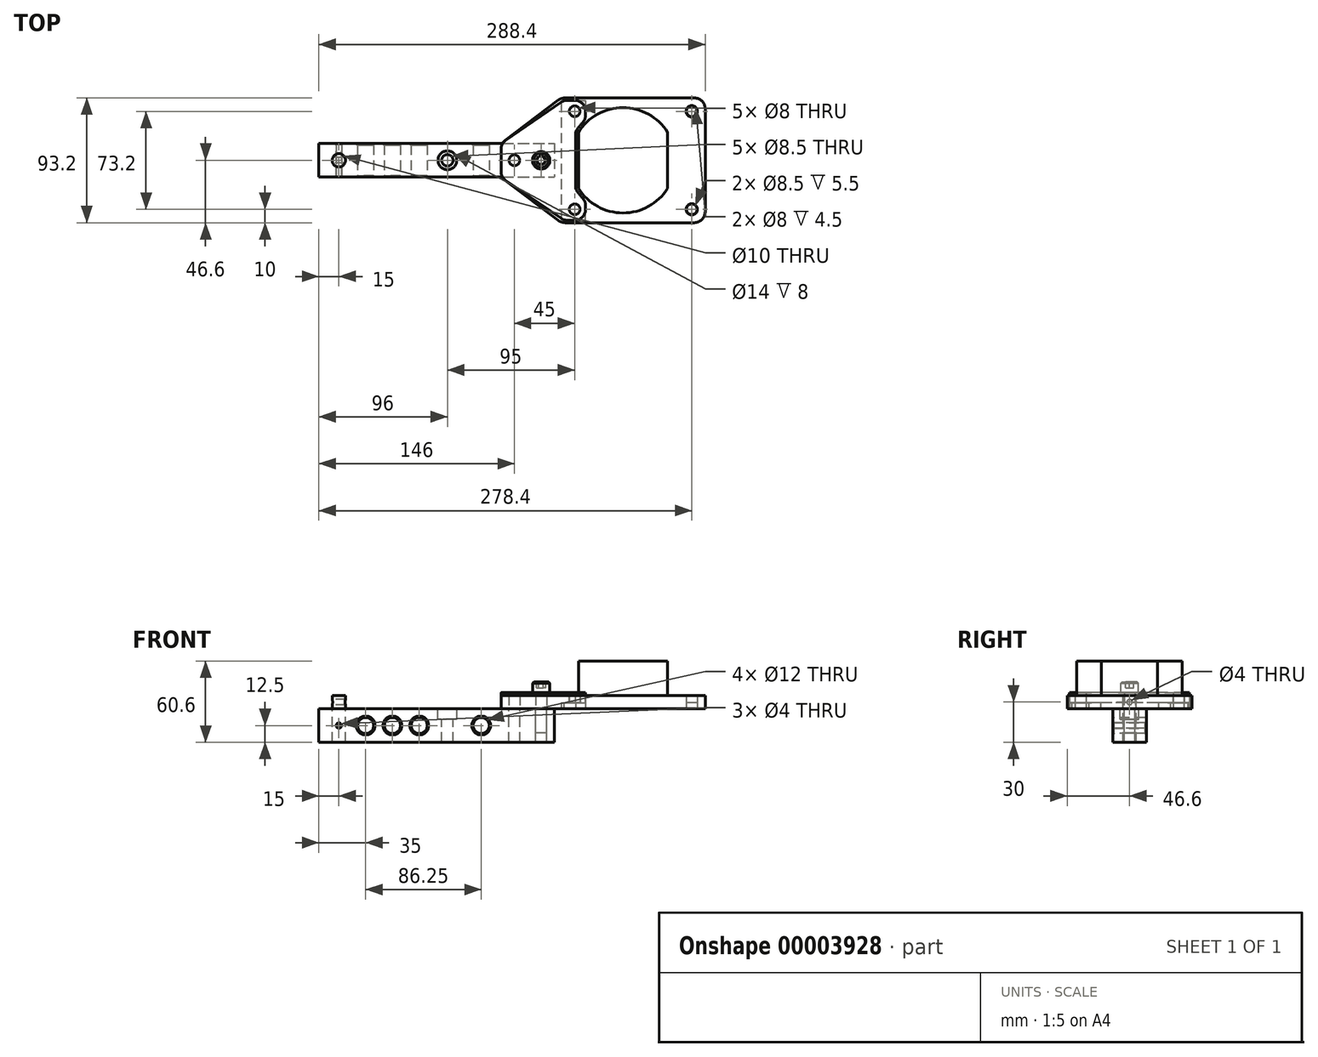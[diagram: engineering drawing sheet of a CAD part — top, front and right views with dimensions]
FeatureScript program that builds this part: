
annotation { "Feature Type Name" : "Feature", "Feature Type Description" : "" }
export const myFeature = defineFeature(function(context is Context, id is Id, definition is map)
    precondition{}
    {
        {
            var Q0;
            Q0=qCreatedBy(makeId("Top.planeOp"),FACE);
            var sketch = newSketch(context, id + "F0", { "sketchPlane" : qUnion([Q0])});
            skLineSegment(sketch, "E0.bottom", {"start": v(-166, 12.5) * mm, "end": v(10, 12.5) * mm});
            skLineSegment(sketch, "E0.left", {"start": v(-166, 12.5) * mm, "end": v(-166, -12.5) * mm});
            skCircle(sketch, "E1", {"center": v(0, 0) * mm, "radius": 4 * mm});
            skCircle(sketch, "E2", {"center": v(-20, 0) * mm, "radius": 4 * mm});
            skLineSegment(sketch, "E3", {"start": v(-166, -12.5) * mm, "end": v(10, -12.5) * mm});
            skLineSegment(sketch, "E4", {"start": v(10, 12.5) * mm, "end": v(10, 0) * mm});
            skLineSegment(sketch, "E5", {"start": v(10, 0) * mm, "end": v(10, -12.5) * mm});
            skCircle(sketch, "E6", {"center": v(-151, 0) * mm, "radius": 5 * mm});
            skCircle(sketch, "E7", {"center": v(-70, 0) * mm, "radius": 4.25 * mm});
            skCircle(sketch, "E8", {"center": v(-70, 0) * mm, "radius": 7 * mm});
            skSolve(sketch);
        }
        {
            var Q0;
            Q0 = qSketchRegion(id + "F0", true);
            var Q1;
            Q1=makeQuery(id+"F0.imprint","IMPRINT",FACE,{"disambiguationData":[TD([[makeQuery(id+"F0.imprint","IMPRINT",EDGE,{"derivedFrom":sQuery(id+"F0.wireOp",EDGE,"E7")}),-1.0]])]});
            extrude(context, id + "F1", {"entities" : qUnion([Q0, Q1]), "oppositeDirection" : true, "depth" : 25 * mm});
        }
        {
            var Q0;
            Q0=makeQuery(id+"F0.imprint","IMPRINT",FACE,{"disambiguationData":[TD([[makeQuery(id+"F0.imprint","IMPRINT",EDGE,{"derivedFrom":sQuery(id+"F0.wireOp",EDGE,"E7")}),-1.0]])]});
            extrude(context, id + "F2", {"entities" : qUnion([Q0]), "operationType" : NewBodyOperationType.REMOVE, "oppositeDirection" : true, "depth" : 8 * mm});
        }
        {
            var Q0;
            Q0=qCreatedBy(makeId("Front.planeOp"),FACE);
            var sketch = newSketch(context, id + "F3", { "sketchPlane" : qUnion([Q0])});
            skLineSegment(sketch, "E9.0", {"start": v(-156, 0) * mm, "end": v(-146, 0) * mm, "construction": true});
            skPoint(sketch, "E10", {"position": v(-151, 0) * mm});
            skCircle(sketch, "E11", {"center": v(-151, -12.5) * mm, "radius": 2 * mm});
            skLineSegment(sketch, "E12", {"start": v(-63, 0) * mm, "end": v(-63, -8) * mm});
            skLineSegment(sketch, "E13", {"start": v(-77, -8) * mm, "end": v(-77, 0) * mm});
            skLineSegment(sketch, "E14.0.0", {"start": v(-77, -8) * mm, "end": v(-63, -8) * mm});
            skLineSegment(sketch, "E15", {"start": v(-65.75, -8) * mm, "end": v(-65.75, -25) * mm});
            skLineSegment(sketch, "E16", {"start": v(-74.25, -25) * mm, "end": v(-74.25, -8) * mm});
            skLineSegment(sketch, "E17", {"start": v(-16, 0) * mm, "end": v(-16, -25) * mm});
            skLineSegment(sketch, "E18", {"start": v(-24, -25) * mm, "end": v(-24, 0) * mm});
            skLineSegment(sketch, "E19", {"start": v(4, 0) * mm, "end": v(4, -25) * mm});
            skLineSegment(sketch, "E20", {"start": v(-4, -25) * mm, "end": v(-4, 0) * mm});
            skCircle(sketch, "E21", {"center": v(-44.75, -12.5) * mm, "radius": 6 * mm});
            skCircle(sketch, "E22", {"center": v(-91, -12.5) * mm, "radius": 6 * mm});
            skCircle(sketch, "E23", {"center": v(-111, -12.5) * mm, "radius": 6 * mm});
            skLineSegment(sketch, "E24.0.0", {"start": v(10, 0) * mm, "end": v(-166, 0) * mm});
            skLineSegment(sketch, "E24.0.2", {"start": v(-166, 0) * mm, "end": v(10, 0) * mm});
            skLineSegment(sketch, "E25.0.0", {"start": v(-166, -25) * mm, "end": v(10, -25) * mm});
            skLineSegment(sketch, "E25.0.2", {"start": v(10, -25) * mm, "end": v(-166, -25) * mm});
            skLineSegment(sketch, "E26.0.1", {"start": v(-166, 0) * mm, "end": v(-166, -25) * mm});
            skLineSegment(sketch, "E26.0.3", {"start": v(-166, -25) * mm, "end": v(-166, 0) * mm});
            skLineSegment(sketch, "E27.0.1", {"start": v(10, 0) * mm, "end": v(10, -25) * mm});
            skLineSegment(sketch, "E27.0.3", {"start": v(10, -25) * mm, "end": v(10, 0) * mm});
            skLineSegment(sketch, "E28", {"start": v(-166, -12.5) * mm, "end": v(10, -12.5) * mm, "construction": true});
            skLineSegment(sketch, "E29", {"start": v(-146, 0) * mm, "end": v(-146, -25) * mm});
            skLineSegment(sketch, "E30", {"start": v(-156, -25) * mm, "end": v(-156, 0) * mm});
            skCircle(sketch, "E31", {"center": v(-131, -12.5) * mm, "radius": 6 * mm});
            skSolve(sketch);
        }
        {
            var Q0;
            Q0=makeQuery(id+"F3.imprint","IMPRINT",FACE,{"disambiguationData":[TD([[makeQuery(id+"F3.imprint","IMPRINT",EDGE,{"derivedFrom":sQuery(id+"F3.wireOp",EDGE,"E11")}),1.0]])]});
            var Q1;
            Q1=makeQuery(id+"F3.imprint","IMPRINT",FACE,{"disambiguationData":[TD([[makeQuery(id+"F3.imprint","IMPRINT",EDGE,{"derivedFrom":sQuery(id+"F3.wireOp",EDGE,"E23")}),1.0]])]});
            var Q2;
            Q2=makeQuery(id+"F3.imprint","IMPRINT",FACE,{"disambiguationData":[TD([[makeQuery(id+"F3.imprint","IMPRINT",EDGE,{"derivedFrom":sQuery(id+"F3.wireOp",EDGE,"E22")}),1.0]])]});
            var Q3;
            Q3=makeQuery(id+"F3.imprint","IMPRINT",FACE,{"disambiguationData":[TD([[makeQuery(id+"F3.imprint","IMPRINT",EDGE,{"derivedFrom":sQuery(id+"F3.wireOp",EDGE,"E21")}),1.0]])]});
            var Q4;
            Q4=makeQuery(id+"F3.imprint","IMPRINT",FACE,{"disambiguationData":[TD([[makeQuery(id+"F3.imprint","IMPRINT",EDGE,{"derivedFrom":sQuery(id+"F3.wireOp",EDGE,"E31")}),1.0]])]});
            extrude(context, id + "F4", {"entities" : qUnion([Q0, Q1, Q2, Q3, Q4]), "operationType" : NewBodyOperationType.REMOVE, "oppositeDirection" : true, "depth" : 25 * mm, "hasSecondDirection" : true, "secondDirectionOppositeDirection" : false, "secondDirectionDepth" : 25 * mm});
        }
        {
            var Q0;
            Q0=qCreatedBy(makeId("Top.planeOp"),FACE);
            var sketch = newSketch(context, id + "F5", { "sketchPlane" : qUnion([Q0])});
            skCircle(sketch, "E32", {"center": v(112.4, 36.6) * mm, "radius": 4.25 * mm});
            skCircle(sketch, "E33", {"center": v(112.4, -36.6) * mm, "radius": 4.25 * mm});
            skCircle(sketch, "E34", {"center": v(25, -36.6) * mm, "radius": 4.25 * mm});
            skCircle(sketch, "E35", {"center": v(25, 36.6) * mm, "radius": 4.25 * mm});
            skCircle(sketch, "E36", {"center": v(0, 0) * mm, "radius": 4.25 * mm});
            skCircle(sketch, "E37", {"center": v(-20, 0) * mm, "radius": 4.25 * mm});
            skLineSegment(sketch, "E38", {"start": v(25, 0) * mm, "end": v(25, 36.6) * mm, "construction": true});
            skLineSegment(sketch, "E39", {"start": v(25, 0) * mm, "end": v(25, -36.6) * mm, "construction": true});
            skLineSegment(sketch, "E40", {"start": v(25, 36.6) * mm, "end": v(112.4, 36.6) * mm, "construction": true});
            skLineSegment(sketch, "E41", {"start": v(112.4, 36.6) * mm, "end": v(112.4, -36.6) * mm, "construction": true});
            skLineSegment(sketch, "E42", {"start": v(112.4, -36.6) * mm, "end": v(25, -36.6) * mm, "construction": true});
            skLineSegment(sketch, "E43.bottom", {"start": v(17.69, 46.6) * mm, "end": v(114.4, 46.6) * mm});
            skLineSegment(sketch, "E43.top", {"start": v(17.69, -46.6) * mm, "end": v(114.4, -46.6) * mm});
            skLineSegment(sketch, "E43.right", {"start": v(122.4, 38.6) * mm, "end": v(122.4, -38.6) * mm});
            skLineSegment(sketch, "E44", {"start": v(15, 46.6) * mm, "end": v(15, 0) * mm, "construction": true});
            skLineSegment(sketch, "E45", {"start": v(15, 0) * mm, "end": v(15, -46.6) * mm, "construction": true});
            skLineSegment(sketch, "E46", {"start": v(-30, 0) * mm, "end": v(-30, 8.52) * mm});
            skLineSegment(sketch, "E47", {"start": v(-30, 0) * mm, "end": v(-30, -8.52) * mm});
            skLineSegment(sketch, "E48", {"start": v(-26.83, 14.9) * mm, "end": v(12.86, 44.98) * mm});
            skLineSegment(sketch, "E49", {"start": v(-26.83, -14.9) * mm, "end": v(12.86, -44.98) * mm});
            skPoint(sketch, "E50.visualSharp", {"position": v(122.4, 46.6) * mm});
            skArc(sketch, "E50.filletArc", {"start": v(122.4, 38.6) * mm, "mid": v(120.06, 44.26) * mm, "end": v(114.4, 46.6) * mm});
            skPoint(sketch, "E51.visualSharp", {"position": v(15, 46.6) * mm});
            skArc(sketch, "E51.filletArc", {"start": v(17.69, 46.6) * mm, "mid": v(15.14, 46.18) * mm, "end": v(12.86, 44.98) * mm});
            skPoint(sketch, "E52.visualSharp", {"position": v(-30, 12.5) * mm});
            skArc(sketch, "E52.filletArc", {"start": v(-26.83, 14.9) * mm, "mid": v(-29.16, 12.08) * mm, "end": v(-30, 8.52) * mm});
            skPoint(sketch, "E53.visualSharp", {"position": v(-30, -12.5) * mm});
            skArc(sketch, "E53.filletArc", {"start": v(-30, -8.52) * mm, "mid": v(-29.16, -12.08) * mm, "end": v(-26.83, -14.9) * mm});
            skPoint(sketch, "E54.visualSharp", {"position": v(15, -46.6) * mm});
            skArc(sketch, "E54.filletArc", {"start": v(12.86, -44.98) * mm, "mid": v(15.14, -46.18) * mm, "end": v(17.69, -46.6) * mm});
            skPoint(sketch, "E55.visualSharp", {"position": v(122.4, -46.6) * mm});
            skArc(sketch, "E55.filletArc", {"start": v(114.4, -46.6) * mm, "mid": v(120.06, -44.26) * mm, "end": v(122.4, -38.6) * mm});
            skSolve(sketch);
        }
        {
            var Q0;
            Q0 = qSketchRegion(id + "F5", true);
            extrude(context, id + "F6", {"entities" : qUnion([Q0]), "depth" : 10 * mm});
        }
        {
            var Q0;
            Q0=qCreatedBy(makeId("Top.planeOp"),FACE);
            var sketch = newSketch(context, id + "F7", { "sketchPlane" : qUnion([Q0])});
            skLineSegment(sketch, "E56", {"start": v(0, 0) * mm, "end": v(133.67, 0) * mm, "construction": true});
            skPoint(sketch, "E57.0", {"position": v(112.4, 36.6) * mm});
            skPoint(sketch, "E57.1", {"position": v(112.4, -36.6) * mm});
            skPoint(sketch, "E57.2", {"position": v(25, -36.6) * mm});
            skPoint(sketch, "E57.3", {"position": v(25, 36.6) * mm});
            skCircle(sketch, "E58", {"center": v(25, 36.6) * mm, "radius": 4 * mm});
            skCircle(sketch, "E59", {"center": v(112.4, 36.6) * mm, "radius": 4 * mm});
            skCircle(sketch, "E60", {"center": v(112.4, -36.6) * mm, "radius": 4 * mm});
            skCircle(sketch, "E61", {"center": v(25, -36.6) * mm, "radius": 4 * mm});
            skLineSegment(sketch, "E62", {"start": v(25, 36.6) * mm, "end": v(112.4, 36.6) * mm, "construction": true});
            skLineSegment(sketch, "E63", {"start": v(25, 36.6) * mm, "end": v(25, 0) * mm, "construction": true});
            skLineSegment(sketch, "E64", {"start": v(25, 0) * mm, "end": v(25, -36.6) * mm, "construction": true});
            skLineSegment(sketch, "E65", {"start": v(25, -36.6) * mm, "end": v(112.4, -36.6) * mm, "construction": true});
            skLineSegment(sketch, "E66", {"start": v(112.4, -36.6) * mm, "end": v(112.4, 36.6) * mm, "construction": true});
            skLineSegment(sketch, "E67.bottom", {"start": v(24.85, 44.75) * mm, "end": v(112.55, 44.75) * mm});
            skLineSegment(sketch, "E67.top", {"start": v(24.85, -44.75) * mm, "end": v(112.55, -44.75) * mm});
            skLineSegment(sketch, "E67.left", {"start": v(16.85, 36.75) * mm, "end": v(16.85, -36.75) * mm});
            skLineSegment(sketch, "E67.right", {"start": v(120.55, 36.75) * mm, "end": v(120.55, -36.75) * mm});
            skPoint(sketch, "E68.visualSharp", {"position": v(16.85, 44.75) * mm});
            skArc(sketch, "E68.filletArc", {"start": v(24.85, 44.75) * mm, "mid": v(19.2, 42.4) * mm, "end": v(16.85, 36.75) * mm});
            skPoint(sketch, "E69.visualSharp", {"position": v(120.55, 44.75) * mm});
            skArc(sketch, "E69.filletArc", {"start": v(120.55, 36.75) * mm, "mid": v(118.2, 42.4) * mm, "end": v(112.55, 44.75) * mm});
            skPoint(sketch, "E70.visualSharp", {"position": v(120.55, -44.75) * mm});
            skArc(sketch, "E70.filletArc", {"start": v(112.55, -44.75) * mm, "mid": v(118.2, -42.4) * mm, "end": v(120.55, -36.75) * mm});
            skPoint(sketch, "E71.visualSharp", {"position": v(16.85, -44.75) * mm});
            skArc(sketch, "E71.filletArc", {"start": v(16.85, -36.75) * mm, "mid": v(19.2, -42.4) * mm, "end": v(24.85, -44.75) * mm});
            skPoint(sketch, "E72", {"position": v(61.1, 0) * mm});
            skCircle(sketch, "E73", {"center": v(61.1, 0) * mm, "radius": 39.35 * mm});
            skLineSegment(sketch, "E74", {"start": v(27.8, 20.97) * mm, "end": v(27.8, -20.97) * mm});
            skLineSegment(sketch, "E75", {"start": v(94.4, 20.97) * mm, "end": v(94.4, -20.97) * mm});
            skSolve(sketch);
        }
        {
            var Q0;
            Q0=makeQuery(id+"F7.imprint","IMPRINT",FACE,{"disambiguationData":[TD([[makeQuery(id+"F7.imprint","IMPRINT",EDGE,{"derivedFrom":sQuery(id+"F7.wireOp",EDGE,"E58")}),-1.0]])]});
            var Q1;
            {var subQ0=sQuery(id+"F7.wireOp",EDGE,"E74");Q1=makeQuery(id+"F7.imprint","IMPRINT",FACE,{"disambiguationData":[TD([[makeQuery(id+"F7.imprint","IMPRINT",EDGE,{"derivedFrom":subQ0}),-1.0]])]});}
            var Q2;
            {var subQ0=sQuery(id+"F7.wireOp",EDGE,"E75");Q2=makeQuery(id+"F7.imprint","IMPRINT",FACE,{"disambiguationData":[TD([[makeQuery(id+"F7.imprint","IMPRINT",EDGE,{"derivedFrom":subQ0}),1.0]])]});}
            var Q3;
            {var subQ1=sQuery(id+"F7.wireOp",EDGE,"E74");Q3=makeQuery(id+"F7.imprint","IMPRINT",FACE,{"disambiguationData":[TD([[makeQuery(id+"F7.imprint","IMPRINT",EDGE,{"derivedFrom":subQ1}),1.0]])]});}
            extrude(context, id + "F8", {"entities" : qUnion([Q0, Q1, Q2, Q3]), "depth" : 4.5 * mm});
        }
        {
            var Q0;
            {var subQ1=sQuery(id+"F7.wireOp",EDGE,"E74");Q0=makeQuery(id+"F7.imprint","IMPRINT",FACE,{"disambiguationData":[TD([[makeQuery(id+"F7.imprint","IMPRINT",EDGE,{"derivedFrom":subQ1}),1.0]])]});}
            extrude(context, id + "F9", {"entities" : qUnion([Q0]), "operationType" : NewBodyOperationType.ADD, "depth" : 35.6 * mm});
        }
        {
            var Q0;
            Q0=qCreatedBy(makeId("Top.planeOp"),FACE);
            var sketch = newSketch(context, id + "F10", { "sketchPlane" : qUnion([Q0])});
            skPoint(sketch, "E76.0", {"position": v(25, 36.6) * mm});
            skPoint(sketch, "E76.1", {"position": v(25, -36.6) * mm});
            skPoint(sketch, "E76.2", {"position": v(0, 0) * mm});
            skCircle(sketch, "E77", {"center": v(0, 0) * mm, "radius": 4 * mm});
            skCircle(sketch, "E78", {"center": v(25, 36.6) * mm, "radius": 4 * mm});
            skCircle(sketch, "E79", {"center": v(25, -36.6) * mm, "radius": 4 * mm});
            skCircle(sketch, "E80", {"center": v(-20, 0) * mm, "radius": 4 * mm});
            skLineSegment(sketch, "E81", {"start": v(-30, 0) * mm, "end": v(-30, 12.5) * mm});
            skLineSegment(sketch, "E82", {"start": v(-30, 0) * mm, "end": v(-30, -12.5) * mm});
            skLineSegment(sketch, "E83", {"start": v(-30, 12.5) * mm, "end": v(16.85, 44.75) * mm});
            skLineSegment(sketch, "E84", {"start": v(16.85, 44.75) * mm, "end": v(33.15, 44.75) * mm});
            skLineSegment(sketch, "E85", {"start": v(-30, 0) * mm, "end": v(40.55, 0) * mm, "construction": true});
            skLineSegment(sketch, "E86", {"start": v(33.15, 44.75) * mm, "end": v(33.15, 0) * mm});
            skLineSegment(sketch, "E87.0.MirrorCS", {"start": v(33.15, -44.75) * mm, "end": v(33.15, 0) * mm});
            skLineSegment(sketch, "E87.1.MirrorCS", {"start": v(-30, -12.5) * mm, "end": v(16.85, -44.75) * mm});
            skLineSegment(sketch, "E87.2.MirrorCS", {"start": v(16.85, -44.75) * mm, "end": v(33.15, -44.75) * mm});
            skArc(sketch, "E88.0.0", {"start": v(94.4, 20.97) * mm, "mid": v(61.1, 39.35) * mm, "end": v(27.8, 20.97) * mm});
            skLineSegment(sketch, "E88.0.1", {"start": v(27.8, 20.97) * mm, "end": v(27.8, -20.97) * mm});
            skArc(sketch, "E88.0.2", {"start": v(27.8, -20.97) * mm, "mid": v(61.1, -39.35) * mm, "end": v(94.4, -20.97) * mm});
            skLineSegment(sketch, "E88.0.3", {"start": v(94.4, 20.97) * mm, "end": v(94.4, -20.97) * mm});
            skLineSegment(sketch, "E88.1.0", {"start": v(24.85, 44.75) * mm, "end": v(112.55, 44.75) * mm});
            skArc(sketch, "E88.1.1", {"start": v(24.85, 44.75) * mm, "mid": v(19.2, 42.4) * mm, "end": v(16.85, 36.75) * mm});
            skLineSegment(sketch, "E88.1.2", {"start": v(16.85, 36.75) * mm, "end": v(16.85, -36.75) * mm});
            skArc(sketch, "E88.1.3", {"start": v(16.85, -36.75) * mm, "mid": v(19.2, -42.4) * mm, "end": v(24.85, -44.75) * mm});
            skLineSegment(sketch, "E88.1.4", {"start": v(24.85, -44.75) * mm, "end": v(112.55, -44.75) * mm});
            skArc(sketch, "E88.1.5", {"start": v(112.55, -44.75) * mm, "mid": v(118.2, -42.4) * mm, "end": v(120.55, -36.75) * mm});
            skLineSegment(sketch, "E88.1.6", {"start": v(120.55, 36.75) * mm, "end": v(120.55, -36.75) * mm});
            skArc(sketch, "E88.1.7", {"start": v(120.55, 36.75) * mm, "mid": v(118.2, 42.4) * mm, "end": v(112.55, 44.75) * mm});
            skLineSegment(sketch, "E89.0", {"start": v(25.8, 21.53) * mm, "end": v(25.8, -21.53) * mm});
            skArc(sketch, "E89.1", {"start": v(96.4, 21.53) * mm, "mid": v(61.1, 41.35) * mm, "end": v(25.8, 21.53) * mm});
            skLineSegment(sketch, "E89.2", {"start": v(96.4, 21.53) * mm, "end": v(96.4, -21.53) * mm});
            skArc(sketch, "E89.3", {"start": v(25.8, -21.53) * mm, "mid": v(61.1, -41.35) * mm, "end": v(96.4, -21.53) * mm});
            skLineSegment(sketch, "E90", {"start": v(14.85, 43.37) * mm, "end": v(14.85, -43.37) * mm});
            skSolve(sketch);
        }
        {
            var Q0;
            Q0=makeQuery(id+"F10.imprint","IMPRINT",FACE,{"disambiguationData":[TD([[makeQuery(id+"F10.imprint","IMPRINT",EDGE,{"derivedFrom":sQuery(id+"F10.wireOp",EDGE,"E77")}),-1.0]])]});
            var Q1;
            {var subQ3=sQuery(id+"F10.wireOp",EDGE,"E84");Q1=makeQuery(id+"F10.imprint","IMPRINT",FACE,{"disambiguationData":[TD([[makeQuery(id+"F10.imprint","IMPRINT",EDGE,{"derivedFrom":subQ3}),-1.0]])]});}
            var Q2;
            Q2=makeQuery(id+"F10.imprint","IMPRINT",FACE,{"disambiguationData":[TD([[makeQuery(id+"F10.imprint","IMPRINT",EDGE,{"derivedFrom":sQuery(id+"F10.wireOp",EDGE,"E78")}),-1.0]])]});
            extrude(context, id + "F11", {"entities" : qUnion([Q0, Q1, Q2]), "depth" : 12 * mm});
        }
        {
            var Q0;
            Q0=makeQuery(id+"F10.imprint","IMPRINT",FACE,{"disambiguationData":[TD([[makeQuery(id+"F10.imprint","IMPRINT",EDGE,{"derivedFrom":sQuery(id+"F10.wireOp",EDGE,"E78")}),-1.0]])]});
            var Q1;
            {var subQ3=sQuery(id+"F10.wireOp",EDGE,"E84");Q1=makeQuery(id+"F10.imprint","IMPRINT",FACE,{"disambiguationData":[TD([[makeQuery(id+"F10.imprint","IMPRINT",EDGE,{"derivedFrom":subQ3}),-1.0]])]});}
            extrude(context, id + "F12", {"entities" : qUnion([Q0, Q1]), "operationType" : NewBodyOperationType.REMOVE, "depth" : 4.5 * mm});
        }
        {
            var Q0;
            Q0=makeQuery(id+"F11.opExtrude","SWEPT_EDGE",EDGE,{"disambiguationData":[OSD([sQuery(id+"F10.wireOp",EDGE,"E87.0.MirrorCS"),sQuery(id+"F10.wireOp",EDGE,"E88.1.4")])]});
            var Q1;
            Q1=makeQuery(id+"F11.opExtrude","SWEPT_EDGE",EDGE,{"disambiguationData":[OSD([sQuery(id+"F10.wireOp",EDGE,"E87.1.MirrorCS"),sQuery(id+"F10.wireOp",EDGE,"E87.2.MirrorCS")])]});
            var Q2;
            Q2=makeQuery(id+"F11.opExtrude","SWEPT_EDGE",EDGE,{"disambiguationData":[OSD([sQuery(id+"F10.wireOp",EDGE,"E81"),sQuery(id+"F10.wireOp",EDGE,"E87.1.MirrorCS")])]});
            var Q3;
            Q3=makeQuery(id+"F11.opExtrude","SWEPT_EDGE",EDGE,{"disambiguationData":[OSD([sQuery(id+"F10.wireOp",EDGE,"E81"),sQuery(id+"F10.wireOp",EDGE,"E83")])]});
            var Q4;
            Q4=makeQuery(id+"F11.opExtrude","SWEPT_EDGE",EDGE,{"disambiguationData":[OSD([sQuery(id+"F10.wireOp",EDGE,"E83"),sQuery(id+"F10.wireOp",EDGE,"E84")])]});
            var Q5;
            Q5=makeQuery(id+"F11.opExtrude","SWEPT_EDGE",EDGE,{"disambiguationData":[OSD([sQuery(id+"F10.wireOp",EDGE,"E86"),sQuery(id+"F10.wireOp",EDGE,"E88.1.0")])]});
            var Q6;
            Q6=makeQuery(id+"F11.opExtrude","SWEPT_EDGE",EDGE,{"disambiguationData":[OSD([sQuery(id+"F10.wireOp",EDGE,"E87.0.MirrorCS"),sQuery(id+"F10.wireOp",EDGE,"E89.3")])]});
            var Q7;
            Q7=makeQuery(id+"F11.opExtrude","SWEPT_EDGE",EDGE,{"disambiguationData":[OSD([sQuery(id+"F10.wireOp",EDGE,"E86"),sQuery(id+"F10.wireOp",EDGE,"E89.1")])]});
            fillet(context, id + "F13", {"entities" : qUnion([Q0, Q1, Q2, Q3, Q4, Q5, Q6, Q7]), "radius" : 8 * mm, "tangentPropagation" : true, "allowEdgeOverflow" : false});
        }
        {
            var Q0;
            Q0=makeQuery(id+"F11.opExtrude","SWEPT_EDGE",EDGE,{"disambiguationData":[OSD([sQuery(id+"F10.wireOp",EDGE,"E89.0"),sQuery(id+"F10.wireOp",EDGE,"E89.3")])]});
            var Q1;
            Q1=makeQuery(id+"F11.opExtrude","SWEPT_EDGE",EDGE,{"disambiguationData":[OSD([sQuery(id+"F10.wireOp",EDGE,"E89.0"),sQuery(id+"F10.wireOp",EDGE,"E89.1")])]});
            fillet(context, id + "F14", {"entities" : qUnion([Q0, Q1]), "radius" : 3 * mm, "tangentPropagation" : true, "allowEdgeOverflow" : false});
        }
        {
            var Q0;
            Q0=makeQuery(id+"F11.opExtrude","CAP_FACE",FACE,{"disambiguationData":[OSD([sQuery(id+"F10.wireOp",EDGE,"E77"),sQuery(id+"F10.wireOp",EDGE,"E78"),sQuery(id+"F10.wireOp",EDGE,"E79"),sQuery(id+"F10.wireOp",EDGE,"E80"),sQuery(id+"F10.wireOp",EDGE,"E81"),sQuery(id+"F10.wireOp",EDGE,"E83"),sQuery(id+"F10.wireOp",EDGE,"E84"),sQuery(id+"F10.wireOp",EDGE,"E86"),sQuery(id+"F10.wireOp",EDGE,"E87.0.MirrorCS"),sQuery(id+"F10.wireOp",EDGE,"E87.1.MirrorCS"),sQuery(id+"F10.wireOp",EDGE,"E87.2.MirrorCS"),sQuery(id+"F10.wireOp",EDGE,"E88.1.0"),sQuery(id+"F10.wireOp",EDGE,"E88.1.4"),sQuery(id+"F10.wireOp",EDGE,"E89.0"),sQuery(id+"F10.wireOp",EDGE,"E89.1"),sQuery(id+"F10.wireOp",EDGE,"E89.3")])],"isStart":false});
            var Q1;
            Q1 = qBodyType(qCreatedBy(id + "F16" ,EDGE), BodyType.WIRE);
            cPlane(context, id + "F15", {"entities" : qUnion([Q0, Q1]), "cplaneType" : CPlaneType.OFFSET, "offset" : 8 * mm, "width" : 150 * mm, "height" : 150 * mm});
        }
        {
            var Q0;
            Q0=qCreatedBy(id+"F15.planeOp",FACE);
            var sketch = newSketch(context, id + "F16", { "sketchPlane" : qUnion([Q0])});
            skCircle(sketch, "E91", {"center": v(0, 0) * mm, "radius": 4 * mm});
            skCircle(sketch, "E92", {"center": v(0, 0) * mm, "radius": 6.5 * mm});
            skCircle(sketch, "E93.cCircle", {"center": v(0, 0) * mm, "radius": 3 * mm, "construction": true});
            skLineSegment(sketch, "E93.0", {"start": v(-1.73, 3) * mm, "end": v(1.73, 3) * mm});
            skLineSegment(sketch, "E93.1", {"start": v(1.73, 3) * mm, "end": v(3.46, 0) * mm});
            skLineSegment(sketch, "E93.2", {"start": v(3.46, 0) * mm, "end": v(1.73, -3) * mm});
            skLineSegment(sketch, "E93.3", {"start": v(1.73, -3) * mm, "end": v(-1.73, -3) * mm});
            skLineSegment(sketch, "E93.4", {"start": v(-1.73, -3) * mm, "end": v(-3.46, 0) * mm});
            skLineSegment(sketch, "E93.5", {"start": v(-3.46, 0) * mm, "end": v(-1.73, 3) * mm});
            skPoint(sketch, "E93.0.midPoint", {"position": v(0, 3) * mm});
            skSolve(sketch);
        }
        {
            var Q0;
            Q0=makeQuery(id+"F16.imprint","IMPRINT",FACE,{"disambiguationData":[TD([[makeQuery(id+"F16.imprint","IMPRINT",EDGE,{"derivedFrom":sQuery(id+"F16.wireOp",EDGE,"E91")}),1.0]])]});
            var Q1;
            Q1=makeQuery(id+"F16.imprint","IMPRINT",FACE,{"disambiguationData":[TD([[makeQuery(id+"F16.imprint","IMPRINT",EDGE,{"derivedFrom":sQuery(id+"F16.wireOp",EDGE,"E93.0")}),-1.0]])]});
            extrude(context, id + "F17", {"entities" : qUnion([Q0, Q1]), "oppositeDirection" : true, "depth" : 38 * mm});
        }
        {
            var Q0;
            Q0=makeQuery(id+"F16.imprint","IMPRINT",FACE,{"disambiguationData":[TD([[makeQuery(id+"F16.imprint","IMPRINT",EDGE,{"derivedFrom":sQuery(id+"F16.wireOp",EDGE,"E91")}),-1.0]])]});
            extrude(context, id + "F18", {"entities" : qUnion([Q0]), "operationType" : NewBodyOperationType.ADD, "oppositeDirection" : true, "depth" : 8 * mm});
        }
        {
            var Q0;
            Q0=makeQuery(id+"F16.imprint","IMPRINT",FACE,{"disambiguationData":[TD([[makeQuery(id+"F16.imprint","IMPRINT",EDGE,{"derivedFrom":sQuery(id+"F16.wireOp",EDGE,"E93.0")}),-1.0]])]});
            extrude(context, id + "F19", {"entities" : qUnion([Q0]), "operationType" : NewBodyOperationType.REMOVE, "oppositeDirection" : true, "depth" : 4.3 * mm});
        }
        {
            var Q0;
            Q0=makeQuery(id+"F18.opExtrude","CAP_EDGE",EDGE,{"disambiguationData":[OSD([sQuery(id+"F16.wireOp",EDGE,"E92")])],"isStart":true});
            chamfer(context, id + "F20", {"entities" : qUnion([Q0]), "width" : 1 * mm, "tangentPropagation" : true});
        }
        {
            var Q0;
            Q0=qCreatedBy(makeId("Front.planeOp"),FACE);
            var sketch = newSketch(context, id + "F21", { "sketchPlane" : qUnion([Q0])});
            skLineSegment(sketch, "E94.0", {"start": v(-156, 0) * mm, "end": v(-146, 0) * mm, "construction": true});
            skLineSegment(sketch, "E95", {"start": v(-156, 0) * mm, "end": v(-156, 10) * mm});
            skLineSegment(sketch, "E96", {"start": v(-156, 0) * mm, "end": v(-156, -25) * mm});
            skPoint(sketch, "E97", {"position": v(-151, 0) * mm});
            skLineSegment(sketch, "E98", {"start": v(-151, 0) * mm, "end": v(-151, 19.88) * mm, "construction": true});
            skLineSegment(sketch, "E99", {"start": v(-151, 0) * mm, "end": v(-151, -36.84) * mm, "construction": true});
            skLineSegment(sketch, "E100", {"start": v(-156, 10) * mm, "end": v(-151, 10) * mm});
            skLineSegment(sketch, "E101", {"start": v(-156, -25) * mm, "end": v(-151, -25) * mm});
            skLineSegment(sketch, "E102", {"start": v(-151, 10) * mm, "end": v(-151, -25) * mm});
            skCircle(sketch, "E103", {"center": v(-151, -12.5) * mm, "radius": 2 * mm});
            skSolve(sketch);
        }
        {
            var Q0;
            Q0=makeQuery(id+"F21.imprint","IMPRINT",FACE,{"disambiguationData":[TD([[makeQuery(id+"F21.imprint","IMPRINT",EDGE,{"derivedFrom":sQuery(id+"F21.wireOp",EDGE,"E95")}),-1.0]])]});
            var Q1;
            {var subQ0=sQuery(id+"F21.wireOp",EDGE,"E102");var subQ1=sQuery(id+"F21.wireOp",EDGE,"a62f2d6b-2e60-48cb-b7ce-1a702a1dbd03");var subQ3=makeQuery(id+"F21.imprint","INTERSECT",VERTEX,{"disambiguationData":[OD(0.0)],"derivedFrom":[subQ1,subQ0]});Q1=makeQuery(id+"F21.imprint","IMPRINT",FACE,{"disambiguationData":[TD([[makeQuery(id+"F21.imprint","IMPRINT",EDGE,{"disambiguationData":[TD([[subQ3,-1.0]])],"derivedFrom":subQ1}),1.0]])]});}
            var Q2;
            Q2=sQuery(id+"F21.wireOp",EDGE,"E99");
            revolve(context, id + "F22", {"entities" : qUnion([Q0, Q1]), "axis" : qUnion([Q2]), "revolveType" : RevolveType.FULL});
        }
        {
            var Q0;
            {var subQ0=sQuery(id+"F21.wireOp",EDGE,"E103");var subQ1=sQuery(id+"F21.wireOp",EDGE,"E102");var subQ3=makeQuery(id+"F21.imprint","INTERSECT",VERTEX,{"disambiguationData":[OD(0.0)],"derivedFrom":[subQ1,subQ0]});Q0=makeQuery(id+"F21.imprint","IMPRINT",FACE,{"disambiguationData":[TD([[makeQuery(id+"F21.imprint","IMPRINT",EDGE,{"disambiguationData":[TD([[subQ3,-1.0]])],"derivedFrom":subQ1}),1.0]])]});}
            var Q1;
            {var subQ0=sQuery(id+"F21.wireOp",EDGE,"E103");var subQ1=sQuery(id+"F21.wireOp",EDGE,"E102");var subQ3=makeQuery(id+"F21.imprint","INTERSECT",VERTEX,{"disambiguationData":[OD(0.0)],"derivedFrom":[subQ1,subQ0]});Q1=makeQuery(id+"F21.imprint","IMPRINT",FACE,{"disambiguationData":[TD([[makeQuery(id+"F21.imprint","IMPRINT",EDGE,{"disambiguationData":[TD([[subQ3,-1.0]])],"derivedFrom":subQ1}),-1.0]])]});}
            extrude(context, id + "F23", {"entities" : qUnion([Q0, Q1]), "operationType" : NewBodyOperationType.REMOVE, "endBound" : BoundingType.THROUGH_ALL, "oppositeDirection" : true, "depth" : 25 * mm, "hasSecondDirection" : true, "secondDirectionBound" : SecondDirectionBoundingType.THROUGH_ALL, "secondDirectionOppositeDirection" : false, "secondDirectionDepth" : 25 * mm});
        }
        {
            var Q0;
            {var subQ0=sQuery(id+"F21.wireOp",EDGE,"E103");var subQ1=sQuery(id+"F21.wireOp",EDGE,"E102");var subQ3=makeQuery(id+"F21.imprint","INTERSECT",VERTEX,{"disambiguationData":[OD(0.0)],"derivedFrom":[subQ1,subQ0]});Q0=makeQuery(id+"F21.imprint","IMPRINT",FACE,{"disambiguationData":[TD([[makeQuery(id+"F21.imprint","IMPRINT",EDGE,{"disambiguationData":[TD([[subQ3,-1.0]])],"derivedFrom":subQ1}),1.0]])]});}
            var Q1;
            {var subQ0=sQuery(id+"F21.wireOp",EDGE,"E103");var subQ1=sQuery(id+"F21.wireOp",EDGE,"E102");var subQ3=makeQuery(id+"F21.imprint","INTERSECT",VERTEX,{"disambiguationData":[OD(0.0)],"derivedFrom":[subQ1,subQ0]});Q1=makeQuery(id+"F21.imprint","IMPRINT",FACE,{"disambiguationData":[TD([[makeQuery(id+"F21.imprint","IMPRINT",EDGE,{"disambiguationData":[TD([[subQ3,-1.0]])],"derivedFrom":subQ1}),-1.0]])]});}
            extrude(context, id + "F24", {"entities" : qUnion([Q0, Q1]), "depth" : 12.5 * mm, "hasSecondDirection" : true, "secondDirectionOppositeDirection" : true, "secondDirectionDepth" : 12.5 * mm});
        }
        {
            var Q0;
            Q0=makeQuery(id+"F24.opExtrude","CAP_EDGE",EDGE,{"disambiguationData":[OSD([sQuery(id+"F21.wireOp",EDGE,"E103")])],"isStart":false});
            var Q1;
            Q1=makeQuery(id+"F24.opExtrude","CAP_EDGE",EDGE,{"disambiguationData":[OSD([sQuery(id+"F21.wireOp",EDGE,"E103")])],"isStart":true});
            chamfer(context, id + "F25", {"entities" : qUnion([Q0, Q1]), "width" : .5 * mm, "tangentPropagation" : true});
        }
        {
            var Q0;
            Q0=makeQuery(id+"F1.opExtrude","SWEPT_FACE",FACE,{"disambiguationData":[OSD([sQuery(id+"F0.wireOp",EDGE,"E0.left")])]});
            var sketch = newSketch(context, id + "F26", { "sketchPlane" : qUnion([Q0])});
            skLineSegment(sketch, "E104.0", {"start": v(-12.5, 0) * mm, "end": v(12.5, 0) * mm, "construction": true});
            skLineSegment(sketch, "E105", {"start": v(0, 0) * mm, "end": v(0, 5) * mm, "construction": true});
            skCircle(sketch, "E106", {"center": v(0, 5) * mm, "radius": 2 * mm});
            skSolve(sketch);
        }
        {
            var Q0;
            Q0=sQuery(id+"F26.wireOp",VERTEX,"E106.center");
            var Q1;
            Q1=makeQuery(id+"F22.opRevolve","SWEPT_BODY",BODY,{"disambiguationData":[OSD([sQuery(id+"F21.wireOp",EDGE,"E95"),sQuery(id+"F21.wireOp",EDGE,"E96"),sQuery(id+"F21.wireOp",EDGE,"E100"),sQuery(id+"F21.wireOp",EDGE,"E101"),sQuery(id+"F21.wireOp",EDGE,"E102"),sQuery(id+"F21.wireOp",EDGE,"E103")])]});
            hole(context, id + "F27", {"style" : HoleStyle.SIMPLE, "holeDiameter" : 4 * mm, "endStyle" : HoleEndStyle.THROUGH, "locations" : qUnion([Q0]), "scope" : qUnion([Q1])});
        }
        {
            var Q0;
            Q0=makeQuery(id+"F4.boolean.opBoolean","INTERSECT",EDGE,{"derivedFrom":[makeQuery(id+"F1.opExtrude","SWEPT_FACE",FACE,{"disambiguationData":[OSD([sQuery(id+"F0.wireOp",EDGE,"E3")])]}),makeQuery(id+"F4.opExtrude","SWEPT_FACE",FACE,{"disambiguationData":[OSD([sQuery(id+"F3.wireOp",EDGE,"E23")])]})]});
            var Q1;
            Q1=makeQuery(id+"F4.boolean.opBoolean","INTERSECT",EDGE,{"derivedFrom":[makeQuery(id+"F1.opExtrude","SWEPT_FACE",FACE,{"disambiguationData":[OSD([sQuery(id+"F0.wireOp",EDGE,"E3")])]}),makeQuery(id+"F4.opExtrude","SWEPT_FACE",FACE,{"disambiguationData":[OSD([sQuery(id+"F3.wireOp",EDGE,"E22")])]})]});
            var Q2;
            Q2=makeQuery(id+"F4.boolean.opBoolean","INTERSECT",EDGE,{"derivedFrom":[makeQuery(id+"F1.opExtrude","SWEPT_FACE",FACE,{"disambiguationData":[OSD([sQuery(id+"F0.wireOp",EDGE,"E3")])]}),makeQuery(id+"F4.opExtrude","SWEPT_FACE",FACE,{"disambiguationData":[OSD([sQuery(id+"F3.wireOp",EDGE,"E21")])]})]});
            var Q3;
            Q3=makeQuery(id+"F4.boolean.opBoolean","INTERSECT",EDGE,{"derivedFrom":[makeQuery(id+"F1.opExtrude","SWEPT_FACE",FACE,{"disambiguationData":[OSD([sQuery(id+"F0.wireOp",EDGE,"E0.bottom")])]}),makeQuery(id+"F4.opExtrude","SWEPT_FACE",FACE,{"disambiguationData":[OSD([sQuery(id+"F3.wireOp",EDGE,"E21")])]})]});
            var Q4;
            Q4=makeQuery(id+"F4.boolean.opBoolean","INTERSECT",EDGE,{"derivedFrom":[makeQuery(id+"F1.opExtrude","SWEPT_FACE",FACE,{"disambiguationData":[OSD([sQuery(id+"F0.wireOp",EDGE,"E0.bottom")])]}),makeQuery(id+"F4.opExtrude","SWEPT_FACE",FACE,{"disambiguationData":[OSD([sQuery(id+"F3.wireOp",EDGE,"E22")])]})]});
            var Q5;
            Q5=makeQuery(id+"F4.boolean.opBoolean","INTERSECT",EDGE,{"derivedFrom":[makeQuery(id+"F1.opExtrude","SWEPT_FACE",FACE,{"disambiguationData":[OSD([sQuery(id+"F0.wireOp",EDGE,"E0.bottom")])]}),makeQuery(id+"F4.opExtrude","SWEPT_FACE",FACE,{"disambiguationData":[OSD([sQuery(id+"F3.wireOp",EDGE,"E23")])]})]});
            var Q6;
            Q6=makeQuery(id+"F4.boolean.opBoolean","INTERSECT",EDGE,{"derivedFrom":[makeQuery(id+"F1.opExtrude","SWEPT_FACE",FACE,{"disambiguationData":[OSD([sQuery(id+"F0.wireOp",EDGE,"E3")])]}),makeQuery(id+"F4.opExtrude","SWEPT_FACE",FACE,{"disambiguationData":[OSD([sQuery(id+"F3.wireOp",EDGE,"E31")])]})]});
            var Q7;
            Q7=makeQuery(id+"F4.boolean.opBoolean","INTERSECT",EDGE,{"derivedFrom":[makeQuery(id+"F1.opExtrude","SWEPT_FACE",FACE,{"disambiguationData":[OSD([sQuery(id+"F0.wireOp",EDGE,"E0.bottom")])]}),makeQuery(id+"F4.opExtrude","SWEPT_FACE",FACE,{"disambiguationData":[OSD([sQuery(id+"F3.wireOp",EDGE,"E31")])]})]});
            chamfer(context, id + "F28", {"entities" : qUnion([Q0, Q1, Q2, Q3, Q4, Q5, Q6, Q7]), "width" : 1 * mm, "tangentPropagation" : true});
        }
    });
